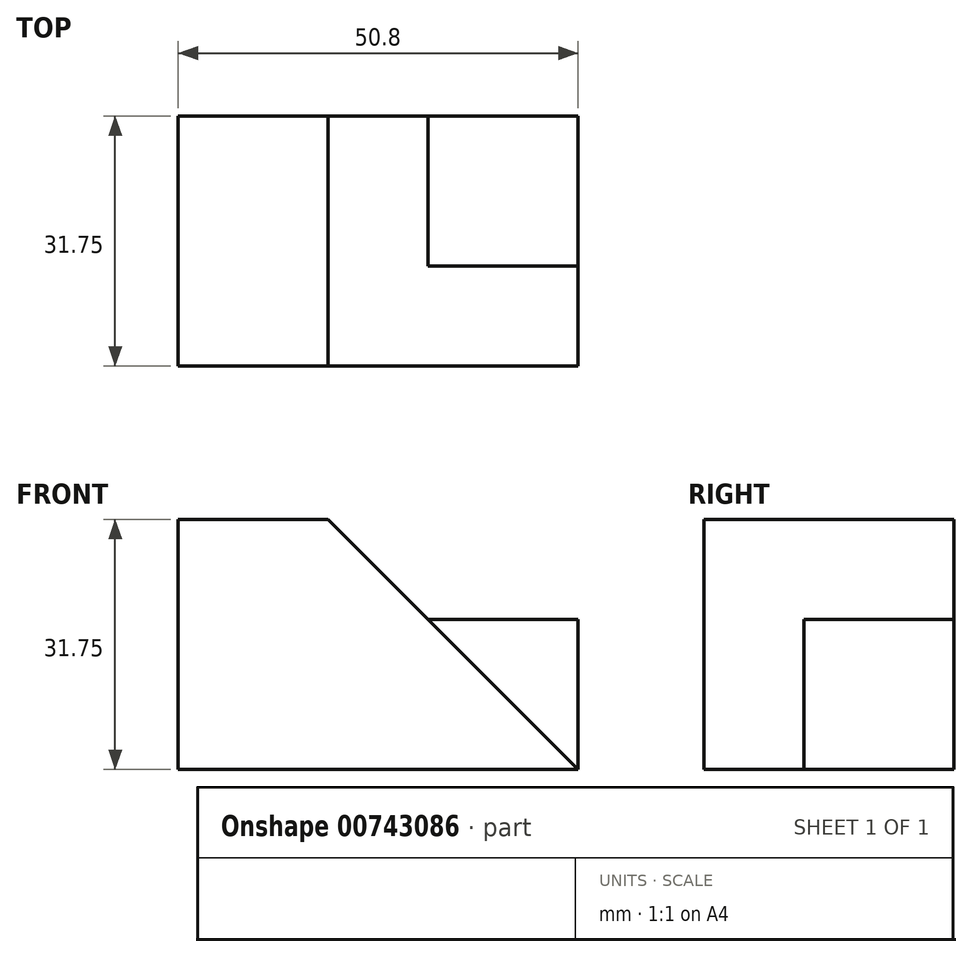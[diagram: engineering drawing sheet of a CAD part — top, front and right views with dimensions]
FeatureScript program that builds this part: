
annotation { "Feature Type Name" : "Feature", "Feature Type Description" : "" }
export const myFeature = defineFeature(function(context is Context, id is Id, definition is map)
    precondition{}
    {
        {
            var Q0;
            Q0=qCreatedBy(makeId("Front.planeOp"),FACE);
            var sketch = newSketch(context, id + "F0", { "sketchPlane" : qUnion([Q0])});
            skLineSegment(sketch, "E0", {"start": v(0, 0) * mm, "end": v(50.8, 0) * mm});
            skLineSegment(sketch, "E1", {"start": v(50.8, 0) * mm, "end": v(50.8, 31.75) * mm});
            skLineSegment(sketch, "E2", {"start": v(50.8, 31.75) * mm, "end": v(0, 31.75) * mm});
            skLineSegment(sketch, "E3", {"start": v(0, 31.75) * mm, "end": v(0, 0) * mm});
            skSolve(sketch);
        }
        {
            var Q0;
            Q0=makeQuery(id+"F0.imprint","IMPRINT",FACE,{"disambiguationData":[TD([[makeQuery(id+"F0.imprint","IMPRINT",EDGE,{"derivedFrom":sQuery(id+"F0.wireOp",EDGE,"E0")}),1.0]])]});
            extrude(context, id + "F1", {"entities" : qUnion([Q0]), "depth" : 31.75 * mm, "offsetDistance" : 25.4 * mm});
        }
        {
            var Q0;
            Q0=makeQuery(id+"F1.opExtrude","CAP_FACE",FACE,{"disambiguationData":[OSD([sQuery(id+"F0.wireOp",EDGE,"E0"),sQuery(id+"F0.wireOp",EDGE,"E1"),sQuery(id+"F0.wireOp",EDGE,"E2"),sQuery(id+"F0.wireOp",EDGE,"E3")])],"isStart":false});
            var sketch = newSketch(context, id + "F2", { "sketchPlane" : qUnion([Q0])});
            skLineSegment(sketch, "E4", {"start": v(19.05, 31.75) * mm, "end": v(50.8, 0) * mm});
            skSolve(sketch);
        }
        {
            var Q0;
            Q0 = qSketchRegion(id + "F2", true);
            var Q1;
            {var subQ0=sQuery(id+"F2.wireOp",EDGE,"E4");Q1=makeQuery(id+"F2.imprint","IMPRINT",FACE,{"disambiguationData":[TD([[makeQuery(id+"F2.imprint","IMPRINT",EDGE,{"derivedFrom":subQ0}),1.0]])]});}
            extrude(context, id + "F3", {"entities" : qUnion([Q0, Q1]), "operationType" : NewBodyOperationType.REMOVE, "oppositeDirection" : true, "depth" : 12.7 * mm, "offsetDistance" : 25.4 * mm});
        }
        {
            var Q0;
            Q0=makeQuery(id+"F1.opExtrude","CAP_FACE",FACE,{"disambiguationData":[OSD([sQuery(id+"F0.wireOp",EDGE,"E0"),sQuery(id+"F0.wireOp",EDGE,"E1"),sQuery(id+"F0.wireOp",EDGE,"E2"),sQuery(id+"F0.wireOp",EDGE,"E3")])],"isStart":true});
            var sketch = newSketch(context, id + "F4", { "sketchPlane" : qUnion([Q0])});
            skLineSegment(sketch, "E5", {"start": v(-19.05, 31.75) * mm, "end": v(-31.75, 19.05) * mm});
            skLineSegment(sketch, "E6", {"start": v(-31.75, 19.05) * mm, "end": v(-50.8, 19.05) * mm});
            skSolve(sketch);
        }
        {
            var Q0;
            {var subQ0=sQuery(id+"F4.wireOp",EDGE,"E5");Q0=makeQuery(id+"F4.imprint","IMPRINT",FACE,{"disambiguationData":[TD([[makeQuery(id+"F4.imprint","IMPRINT",EDGE,{"derivedFrom":subQ0}),-1.0]])]});}
            extrude(context, id + "F5", {"entities" : qUnion([Q0]), "operationType" : NewBodyOperationType.REMOVE, "oppositeDirection" : true, "depth" : 25.4 * mm, "offsetDistance" : 25.4 * mm});
        }
    });
